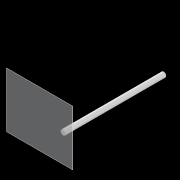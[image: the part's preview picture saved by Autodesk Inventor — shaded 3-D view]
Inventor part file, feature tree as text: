
AUTODESK INVENTOR PART (.ipt)
format: ipt  version: 2021 (Build 250183000, 183)  size: 77,824 bytes
history: native  units: mm
features: thread x2, other x2, plane x1, extrude x1, sketch x1, reference x1
ambient origin geometry x8: Origin, YZ Plane, XZ Plane, XY Plane, X Axis, Y Axis, Z Axis, Center Point
bodies: Solid1 (feature_tree)
feature tree (8):
  plane  "Work Plane1"
  extrude  "Extrusion1"  Depth=330.0mm
  thread  "Thread1"  [1 undecoded]
  thread  "Thread2"  [1 undecoded]
  sketch  "Sketch1"  dims[d0=330.0mm d1=0.0mm d2=330.0mm d3=260.0mm d4=60.0mm d5=0.0mm]
  reference  "Reference2"
  other  "Subensamble_mesa.iam"
  other  "Base soporte tubos:2"
note: 2 required parameter values undecoded (feature->parameter linkage not recoverable at this tier; creation-order binding heuristic only, values carry confidence <= 0.55)
